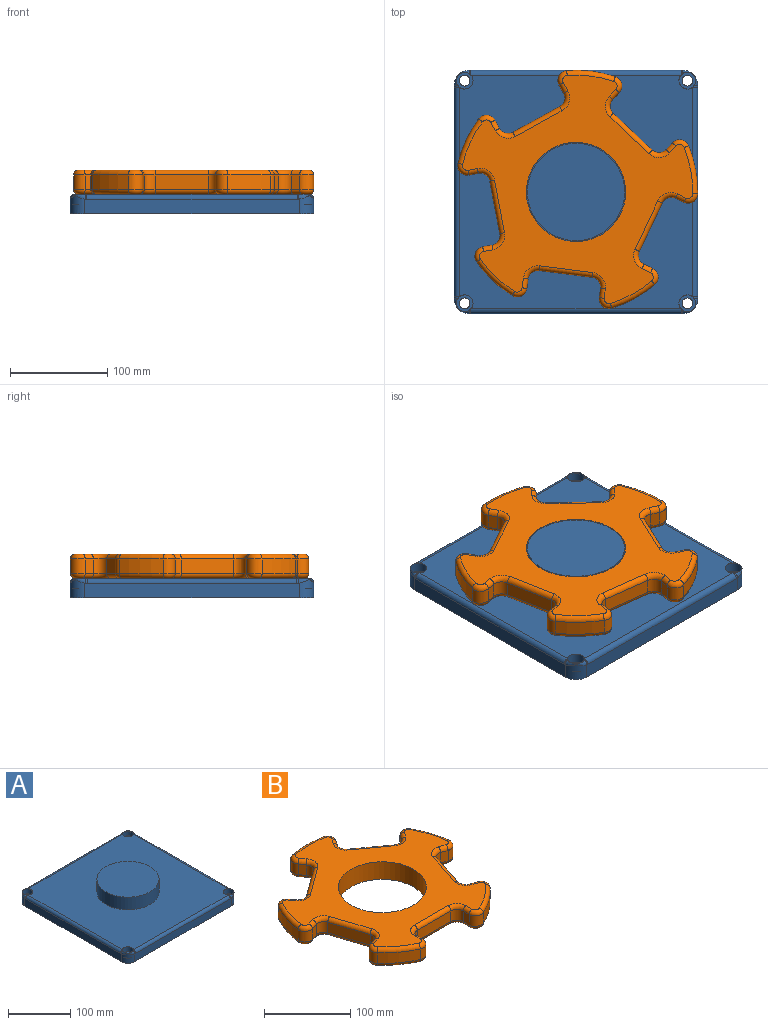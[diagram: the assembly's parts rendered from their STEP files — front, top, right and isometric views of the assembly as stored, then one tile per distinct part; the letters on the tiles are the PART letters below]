
ASSEMBLY  parts=2 mates=1
PART A: 40 faces, bbox 250x250x45 mm
  f0: plane 220x15.24mm, normal (1,0,0), area 3300.4mm2, adj f5,f8,f11,f33,f35,f37
  f1: plane 220x15.22mm, normal (0,1,0), area 3300.3mm2, adj f5,f8,f9,f34,f36,f38
  f2: plane 220x15.24mm, normal (-1,0,0), area 3300.4mm2, adj f5,f9,f10,f26,f28,f30
  f3: plane 220x15.22mm, normal (0,-1,0), area 3300.3mm2, adj f5,f10,f11,f25,f27,f29
  f4: plane 240x240mm, normal (0,0,1), area 49029mm2, adj f6,f14,f17,f20,f23,f27,f28,f35
  f5: plane 250x250mm, normal (0,0,-1), area 61926.7mm2, adj f0,f1,f2,f3,f8,f9,f10,f11
  f6: cylinder r=50mm len=100mm, axis (0,0,-1), area 7854mm2, adj f4,f7
  f7: plane 100x100mm, normal (0,0,1), area 7854mm2, adj f6
  f8: cylinder r=15mm len=18.74mm, axis (0,0,-1), area 396.9mm2, adj f0,f1,f5,f39
  f9: cylinder r=15mm len=18.74mm, axis (0,0,1), area 396.9mm2, adj f1,f2,f5,f32
  f10: cylinder r=15mm len=18.74mm, axis (0,0,-1), area 396.9mm2, adj f2,f3,f5,f24
  f11: cylinder r=15mm len=18.74mm, axis (0,0,1), area 396.9mm2, adj f0,f3,f5,f31
  f12: cylinder r=5.5mm len=11mm, axis (0,0,1), area 345.6mm2, adj f5,f13
  f13: plane 17.25x17.25mm, normal (0,0,1), area 138.7mm2, adj f12,f14
  f14: cylinder r=8.62mm len=17.25mm, axis (0,0,1), area 541.9mm2, adj f4,f13,f30,f32,f34
  f15: cylinder r=5.5mm len=11mm, axis (0,0,1), area 345.6mm2, adj f5,f16
  f16: plane 17.25x17.25mm, normal (0,0,1), area 138.7mm2, adj f15,f17
  f17: cylinder r=8.62mm len=17.25mm, axis (0,0,1), area 541.9mm2, adj f4,f16,f37,f38,f39
  f18: cylinder r=5.5mm len=11mm, axis (0,0,1), area 345.6mm2, adj f5,f19
  f19: plane 17.25x17.25mm, normal (0,0,1), area 138.7mm2, adj f18,f20
  f20: cylinder r=8.62mm len=17.25mm, axis (0,0,1), area 541.9mm2, adj f4,f19,f29,f31,f33
  f21: cylinder r=5.5mm len=11mm, axis (0,0,1), area 345.6mm2, adj f5,f22
  f22: plane 17.25x17.25mm, normal (0,0,1), area 138.7mm2, adj f21,f23
  f23: cylinder r=8.62mm len=17.25mm, axis (0,0,1), area 541.9mm2, adj f4,f22,f24,f25,f26
  f24: bspline ~15.95x15.9mm, area 86.8mm2, adj f10,f23,f25,f26
  f25: bspline ~5x5mm, area 11.3mm2, adj f3,f23,f24,f27
  f26: bspline ~5x5mm, area 11.8mm2, adj f2,f23,f24,f28
  f27: cylinder r=5mm len=215.78mm, axis (-1,0,0), area 1694.7mm2, adj f3,f4,f25,f29
  f28: cylinder r=5mm len=215.58mm, axis (0,1,0), area 1693.2mm2, adj f2,f4,f26,f30
  f29: bspline ~5x5mm, area 11.3mm2, adj f3,f20,f27,f31
  f30: bspline ~5x5mm, area 11.8mm2, adj f2,f14,f28,f32
  f31: bspline ~15.95x15.9mm, area 86.9mm2, adj f11,f20,f29,f33
  f32: bspline ~15.95x15.9mm, area 86.9mm2, adj f9,f14,f30,f34
  f33: bspline ~5x5mm, area 11.8mm2, adj f0,f20,f31,f35
  f34: bspline ~5x5mm, area 11.3mm2, adj f1,f14,f32,f36
  f35: cylinder r=5mm len=215.58mm, axis (0,-1,0), area 1693.2mm2, adj f0,f4,f33,f37
  f36: cylinder r=5mm len=215.78mm, axis (1,0,0), area 1694.7mm2, adj f1,f4,f34,f38
  f37: bspline ~5x5mm, area 11.8mm2, adj f0,f17,f35,f39
  f38: bspline ~5x5mm, area 11.3mm2, adj f1,f17,f36,f39
  f39: bspline ~15.95x15.9mm, area 86.8mm2, adj f8,f17,f37,f38
PART B: 123 faces, bbox 268.9x258.5x25 mm
  f0: plane 238.57x229.73mm, normal (0,0,1), area 21505.7mm2, adj f6,f43,f44,f45,f46,f47,f48,f49
  f1: plane 238.57x229.73mm, normal (0,0,-1), area 21505.7mm2, adj f6,f83,f84,f85,f86,f87,f88,f89
  f2: cylinder r=125mm len=40.68mm, axis (0,0,-1), area 759.5mm2, adj f13,f42,f51,f91
  f3: cylinder r=125mm len=47.82mm, axis (0,0,-1), area 759.5mm2, adj f35,f41,f67,f107
  f4: cylinder r=125mm len=50.29mm, axis (0,0,-1), area 759.5mm2, adj f28,f34,f82,f122
  f5: cylinder r=125mm len=47.82mm, axis (0,0,-1), area 759.5mm2, adj f21,f27,f66,f106
  f6: cylinder r=51mm len=102mm, axis (0,0,-1), area 8011.1mm2, adj f0,f1
  f7: cylinder r=125mm len=40.68mm, axis (0,0,-1), area 759.5mm2, adj f14,f20,f50,f90
  f8: plane 15x9.73mm, normal (-1,0,0), area 146mm2, adj f11,f14,f46,f86
  f9: plane 55x15mm, normal (0,-1,0), area 825mm2, adj f11,f12,f43,f83
  f10: plane 15x9.73mm, normal (1,0,0), area 146mm2, adj f12,f13,f47,f87
  f11: cylinder r=10mm len=15mm, axis (0,0,-1), area 235.6mm2, adj f8,f9,f44,f84
  f12: cylinder r=10mm len=15mm, axis (0,0,-1), area 235.6mm2, adj f9,f10,f45,f85
  f13: cylinder r=10mm len=15mm, axis (0,0,-1), area 299.5mm2, adj f2,f10,f49,f89
  f14: cylinder r=10mm len=15mm, axis (0,0,-1), area 299.5mm2, adj f7,f8,f48,f88
  f15: plane 15x9.26mm, normal (-0.31,-0.95,0), area 146mm2, adj f18,f21,f62,f102
  f16: plane 52.31x17mm, normal (0.95,-0.31,0), area 825mm2, adj f18,f19,f58,f98
  f17: plane 15x9.26mm, normal (0.31,0.95,0), area 146mm2, adj f19,f20,f54,f94
  f18: cylinder r=10mm len=15mm, axis (0,0,-1), area 235.6mm2, adj f15,f16,f60,f100
  f19: cylinder r=10mm len=15mm, axis (0,0,-1), area 235.6mm2, adj f16,f17,f56,f96
  f20: cylinder r=10mm len=16.25mm, axis (0,0,-1), area 299.5mm2, adj f7,f17,f52,f92
  f21: cylinder r=10mm len=15mm, axis (0,0,-1), area 299.5mm2, adj f5,f15,f64,f104
  f22: plane 15x7.87mm, normal (0.81,-0.59,0), area 146mm2, adj f25,f28,f78,f118
  f23: plane 44.5x32.33mm, normal (0.59,0.81,0), area 825mm2, adj f25,f26,f74,f114
  f24: plane 15x7.87mm, normal (-0.81,0.59,0), area 146mm2, adj f26,f27,f70,f110
  f25: cylinder r=10mm len=15mm, axis (0,0,-1), area 235.6mm2, adj f22,f23,f76,f116
  f26: cylinder r=10mm len=15mm, axis (0,0,-1), area 235.6mm2, adj f23,f24,f72,f112
  f27: cylinder r=10mm len=16.78mm, axis (0,0,-1), area 299.5mm2, adj f5,f24,f68,f108
  f28: cylinder r=10mm len=15.67mm, axis (0,0,-1), area 299.5mm2, adj f4,f22,f80,f120
  f29: plane 15x7.87mm, normal (0.81,0.59,0), area 146mm2, adj f32,f35,f71,f111
  f30: plane 44.5x32.33mm, normal (-0.59,0.81,0), area 825mm2, adj f32,f33,f75,f115
  f31: plane 15x7.87mm, normal (-0.81,-0.59,0), area 146mm2, adj f33,f34,f79,f119
  f32: cylinder r=10mm len=15mm, axis (0,0,-1), area 235.6mm2, adj f29,f30,f73,f113
  f33: cylinder r=10mm len=15mm, axis (0,0,-1), area 235.6mm2, adj f30,f31,f77,f117
  f34: cylinder r=10mm len=15.67mm, axis (0,0,-1), area 299.5mm2, adj f4,f31,f81,f121
  f35: cylinder r=10mm len=16.78mm, axis (0,0,-1), area 299.5mm2, adj f3,f29,f69,f109
  f36: plane 15x9.26mm, normal (-0.31,0.95,0), area 146mm2, adj f39,f42,f55,f95
  f37: plane 52.31x17mm, normal (-0.95,-0.31,0), area 825mm2, adj f39,f40,f59,f99
  f38: plane 15x9.26mm, normal (0.31,-0.95,0), area 146mm2, adj f40,f41,f63,f103
  f39: cylinder r=10mm len=15mm, axis (0,0,-1), area 235.6mm2, adj f36,f37,f57,f97
  f40: cylinder r=10mm len=15mm, axis (0,0,-1), area 235.6mm2, adj f37,f38,f61,f101
  f41: cylinder r=10mm len=15mm, axis (0,0,-1), area 299.5mm2, adj f3,f38,f65,f105
  f42: cylinder r=10mm len=16.25mm, axis (0,0,-1), area 299.5mm2, adj f2,f36,f53,f93
  f43: cylinder r=5mm len=55mm, axis (1,0,0), area 432mm2, adj f0,f9,f44,f45
  f44: torus R=15mm, axis (0,0,1), area 145.8mm2, adj f0,f11,f43,f46
  f45: torus R=15mm, axis (0,0,1), area 145.8mm2, adj f0,f12,f43,f47
  f46: cylinder r=5mm len=9.73mm, axis (0,-1,0), area 76.4mm2, adj f0,f8,f44,f48
  f47: cylinder r=5mm len=9.73mm, axis (0,1,0), area 76.4mm2, adj f0,f10,f45,f49
  f48: torus R=5mm, axis (0,0,1), area 128.3mm2, adj f0,f14,f46,f50
  f49: torus R=5mm, axis (0,0,1), area 128.3mm2, adj f0,f13,f47,f51
  f50: torus R=120mm, axis (0,0,1), area 391.9mm2, adj f0,f7,f48,f52
  f51: torus R=120mm, axis (0,0,1), area 391.9mm2, adj f0,f2,f49,f53
  f52: torus R=5mm, axis (0,0,1), area 128.3mm2, adj f0,f20,f50,f54
  f53: torus R=5mm, axis (0,0,1), area 128.3mm2, adj f0,f42,f51,f55
  f54: cylinder r=5mm len=10.8mm, axis (-0.95,0.31,0), area 76.4mm2, adj f0,f17,f52,f56
  f55: cylinder r=5mm len=10.8mm, axis (-0.95,-0.31,0), area 76.4mm2, adj f0,f36,f53,f57
  f56: torus R=15mm, axis (0,0,1), area 145.8mm2, adj f0,f19,f54,f58
  f57: torus R=15mm, axis (0,0,1), area 145.8mm2, adj f0,f39,f55,f59
  f58: cylinder r=5mm len=53.85mm, axis (0.31,0.95,0), area 432mm2, adj f0,f16,f56,f60
  f59: cylinder r=5mm len=53.85mm, axis (0.31,-0.95,0), area 432mm2, adj f0,f37,f57,f61
  f60: torus R=15mm, axis (0,0,1), area 145.8mm2, adj f0,f18,f58,f62
  f61: torus R=15mm, axis (0,0,1), area 145.8mm2, adj f0,f40,f59,f63
  f62: cylinder r=5mm len=10.8mm, axis (0.95,-0.31,0), area 76.4mm2, adj f0,f15,f60,f64
  f63: cylinder r=5mm len=10.8mm, axis (0.95,0.31,0), area 76.4mm2, adj f0,f38,f61,f65
  f64: torus R=5mm, axis (0,0,1), area 128.3mm2, adj f0,f21,f62,f66
  f65: torus R=5mm, axis (0,0,1), area 128.3mm2, adj f0,f41,f63,f67
  f66: torus R=120mm, axis (0,0,1), area 391.9mm2, adj f0,f5,f64,f68
  f67: torus R=120mm, axis (0,0,1), area 391.9mm2, adj f0,f3,f65,f69
  f68: torus R=5mm, axis (0,0,1), area 128.3mm2, adj f0,f27,f66,f70
  f69: torus R=5mm, axis (0,0,1), area 128.3mm2, adj f0,f35,f67,f71
  f70: cylinder r=5mm len=10.81mm, axis (-0.59,-0.81,0), area 76.4mm2, adj f0,f24,f68,f72
  f71: cylinder r=5mm len=10.81mm, axis (-0.59,0.81,0), area 76.4mm2, adj f0,f29,f69,f73
  f72: torus R=15mm, axis (0,0,1), area 145.8mm2, adj f0,f26,f70,f74
  f73: torus R=15mm, axis (0,0,1), area 145.8mm2, adj f0,f32,f71,f75
  f74: cylinder r=5mm len=47.44mm, axis (-0.81,0.59,0), area 432mm2, adj f0,f23,f72,f76
  f75: cylinder r=5mm len=47.44mm, axis (-0.81,-0.59,0), area 432mm2, adj f0,f30,f73,f77
  f76: torus R=15mm, axis (0,0,1), area 145.8mm2, adj f0,f25,f74,f78
  f77: torus R=15mm, axis (0,0,1), area 145.8mm2, adj f0,f33,f75,f79
  f78: cylinder r=5mm len=10.81mm, axis (0.59,0.81,0), area 76.4mm2, adj f0,f22,f76,f80
  f79: cylinder r=5mm len=10.81mm, axis (0.59,-0.81,0), area 76.4mm2, adj f0,f31,f77,f81
  f80: torus R=5mm, axis (0,0,1), area 128.3mm2, adj f0,f28,f78,f82
  f81: torus R=5mm, axis (0,0,1), area 128.3mm2, adj f0,f34,f79,f82
  f82: torus R=120mm, axis (0,0,1), area 391.9mm2, adj f0,f4,f80,f81
  f83: cylinder r=5mm len=55mm, axis (-1,0,0), area 432mm2, adj f1,f9,f84,f85
  f84: torus R=15mm, axis (0,0,1), area 145.8mm2, adj f1,f11,f83,f86
  f85: torus R=15mm, axis (0,0,1), area 145.8mm2, adj f1,f12,f83,f87
  f86: cylinder r=5mm len=9.73mm, axis (0,1,0), area 76.4mm2, adj f1,f8,f84,f88
  f87: cylinder r=5mm len=9.73mm, axis (0,-1,0), area 76.4mm2, adj f1,f10,f85,f89
  f88: torus R=5mm, axis (0,0,1), area 128.3mm2, adj f1,f14,f86,f90
  f89: torus R=5mm, axis (0,0,1), area 128.3mm2, adj f1,f13,f87,f91
  f90: torus R=120mm, axis (0,0,1), area 391.9mm2, adj f1,f7,f88,f92
  f91: torus R=120mm, axis (0,0,1), area 391.9mm2, adj f1,f2,f89,f93
  f92: torus R=5mm, axis (0,0,1), area 128.3mm2, adj f1,f20,f90,f94
  f93: torus R=5mm, axis (0,0,1), area 128.3mm2, adj f1,f42,f91,f95
  f94: cylinder r=5mm len=10.8mm, axis (0.95,-0.31,0), area 76.4mm2, adj f1,f17,f92,f96
  f95: cylinder r=5mm len=10.8mm, axis (0.95,0.31,0), area 76.4mm2, adj f1,f36,f93,f97
  f96: torus R=15mm, axis (0,0,1), area 145.8mm2, adj f1,f19,f94,f98
  f97: torus R=15mm, axis (0,0,1), area 145.8mm2, adj f1,f39,f95,f99
  f98: cylinder r=5mm len=53.85mm, axis (-0.31,-0.95,0), area 432mm2, adj f1,f16,f96,f100
  f99: cylinder r=5mm len=53.85mm, axis (-0.31,0.95,0), area 432mm2, adj f1,f37,f97,f101
  f100: torus R=15mm, axis (0,0,1), area 145.8mm2, adj f1,f18,f98,f102
  f101: torus R=15mm, axis (0,0,1), area 145.8mm2, adj f1,f40,f99,f103
  f102: cylinder r=5mm len=10.8mm, axis (-0.95,0.31,0), area 76.4mm2, adj f1,f15,f100,f104
  f103: cylinder r=5mm len=10.8mm, axis (-0.95,-0.31,0), area 76.4mm2, adj f1,f38,f101,f105
  f104: torus R=5mm, axis (0,0,1), area 128.3mm2, adj f1,f21,f102,f106
  f105: torus R=5mm, axis (0,0,1), area 128.3mm2, adj f1,f41,f103,f107
  f106: torus R=120mm, axis (0,0,1), area 391.9mm2, adj f1,f5,f104,f108
  f107: torus R=120mm, axis (0,0,1), area 391.9mm2, adj f1,f3,f105,f109
  f108: torus R=5mm, axis (0,0,1), area 128.3mm2, adj f1,f27,f106,f110
  f109: torus R=5mm, axis (0,0,1), area 128.3mm2, adj f1,f35,f107,f111
  f110: cylinder r=5mm len=10.81mm, axis (0.59,0.81,0), area 76.4mm2, adj f1,f24,f108,f112
  f111: cylinder r=5mm len=10.81mm, axis (0.59,-0.81,0), area 76.4mm2, adj f1,f29,f109,f113
  f112: torus R=15mm, axis (0,0,1), area 145.8mm2, adj f1,f26,f110,f114
  f113: torus R=15mm, axis (0,0,1), area 145.8mm2, adj f1,f32,f111,f115
  f114: cylinder r=5mm len=47.44mm, axis (0.81,-0.59,0), area 432mm2, adj f1,f23,f112,f116
  f115: cylinder r=5mm len=47.44mm, axis (0.81,0.59,0), area 432mm2, adj f1,f30,f113,f117
  f116: torus R=15mm, axis (0,0,1), area 145.8mm2, adj f1,f25,f114,f118
  f117: torus R=15mm, axis (0,0,1), area 145.8mm2, adj f1,f33,f115,f119
  f118: cylinder r=5mm len=10.81mm, axis (-0.59,-0.81,0), area 76.4mm2, adj f1,f22,f116,f120
  f119: cylinder r=5mm len=10.81mm, axis (-0.59,0.81,0), area 76.4mm2, adj f1,f31,f117,f121
  f120: torus R=5mm, axis (0,0,1), area 128.3mm2, adj f1,f28,f118,f122
  f121: torus R=5mm, axis (0,0,1), area 128.3mm2, adj f1,f34,f119,f122
  f122: torus R=120mm, axis (0,0,1), area 391.9mm2, adj f1,f4,f120,f121
PLACE A at identity fixed
PLACE B rot(axis=(0,0,-1),79.3deg) t=(0,0,0)mm
MATE revolute B.f2 <-> A.f6  axis (0,0,-1) through (0,0,45)mm
